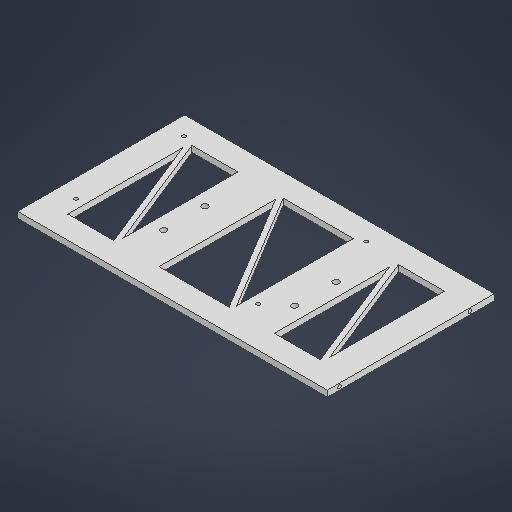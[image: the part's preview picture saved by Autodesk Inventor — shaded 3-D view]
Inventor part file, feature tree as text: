
AUTODESK INVENTOR PART (.ipt)
format: ipt  version: 2025.1 (Build 291241000, 241)  size: 455,680 bytes
history: native  units: in
note: dims shown in document units (in); Inventor stores cm internally (conversion verified against a paired STEP export)
features: extrude x5, sketch x5, plane x3, mirror x2, projected_geometry x1
ambient origin geometry x8: Origin, YZ Plane, XZ Plane, XY Plane, X Axis, Y Axis, Z Axis, Center Point
bodies: Solid1 (feature_tree)
feature tree (16):
  extrude  "Extrusion1"  Depth=0.3937in
  extrude  "Extrusion2"  Depth=0.1181in
  plane  "Work Plane1"
  mirror  "Mirror1"
  extrude  "Extrusion3"  Depth=0.2362in TaperAngle=0.0deg
  sketch  "Sketch4"  dims[d8=0.3937in d9=0.0in d10=0.0984in d11=0.0in]
  plane  "Work Plane2"
  extrude  "Extrusion4"  Depth=0.0984in TaperAngle=0.0deg
  mirror  "Mirror2"
  extrude  "Extrusion5"  Depth=3.937in
  sketch  "Sketch1"  dims[d0=0.3937in d1=0.0in d2=0.7874in]
  sketch  "Sketch2"  dims[d3=0.7874in d4=0.1181in]
  sketch  "Sketch3"  dims[d5=0.1181in d6=0.2362in d7=0.0in]
  plane  "Work Plane3"
  sketch  "Sketch6"  dims[d12=2.3622in d13=3.937in d14=1.5748in d15=1.378in d16=0.0787in d17=0.0787in d18=0.0787in d19=0.0787in d20=0.0787in d21=0.0787in d22=0.0in d23=0.0in]
  projected_geometry  "Projected Loop2"
